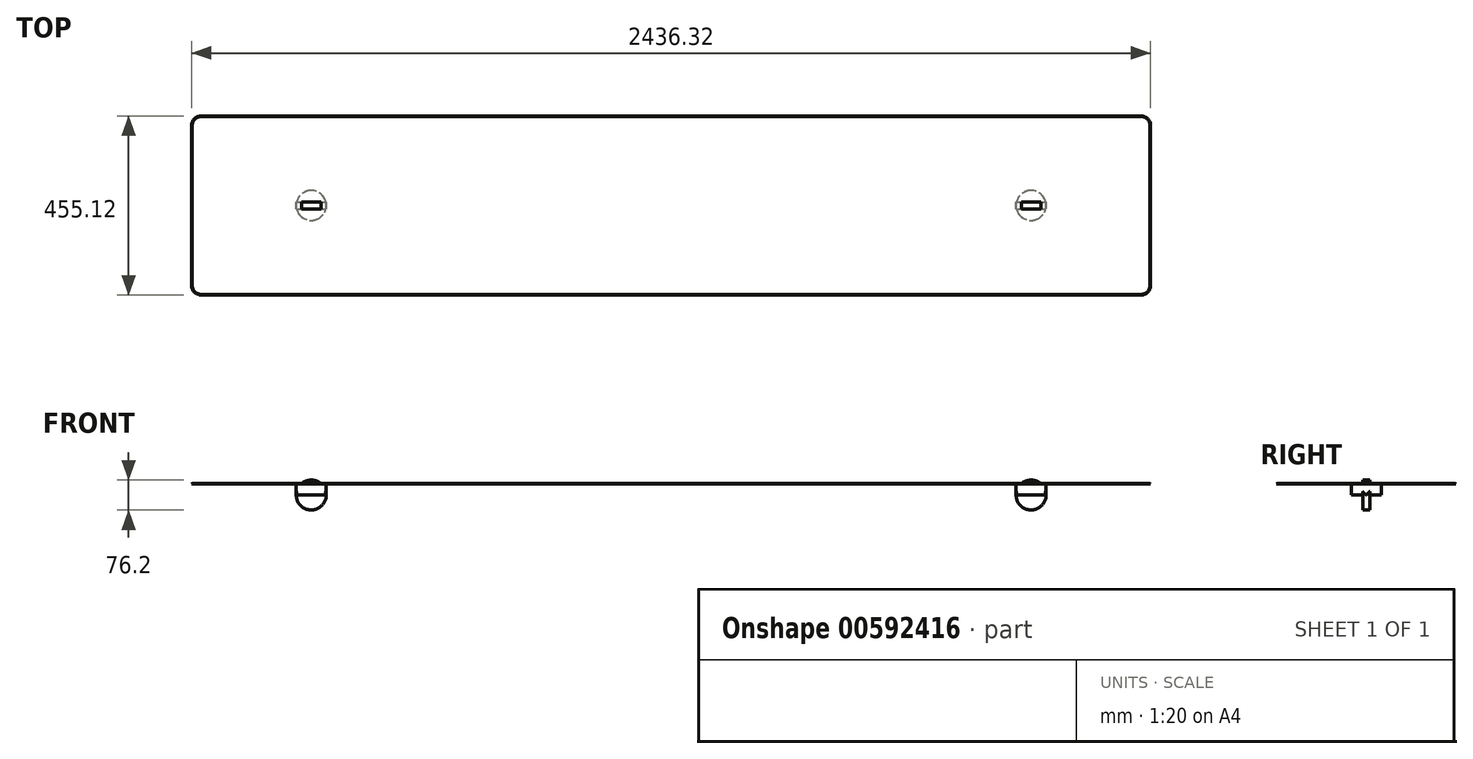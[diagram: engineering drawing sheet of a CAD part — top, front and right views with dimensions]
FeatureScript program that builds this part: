
annotation { "Feature Type Name" : "Feature", "Feature Type Description" : "" }
export const myFeature = defineFeature(function(context is Context, id is Id, definition is map)
    precondition{}
    {
        {
            assignVariable(context, id + "F0", {"name" : "depth", "anyValue" : 18});
        }
        {
            assignVariable(context, id + "F1", {"name" : "height", "anyValue" : 29});
        }
        {
            var Q0;
            Q0=qCreatedBy(makeId("Top.planeOp"),FACE);
            var sketch = newSketch(context, id + "F2", { "sketchPlane" : qUnion([Q0])});
            skLineSegment(sketch, "E0.bottom", {"start": v(1219.2, -228.6) * mm, "end": v(-1219.2, -228.6) * mm});
            skLineSegment(sketch, "E0.top", {"start": v(1219.2, 228.6) * mm, "end": v(-1219.2, 228.6) * mm});
            skLineSegment(sketch, "E0.left", {"start": v(1219.2, -228.6) * mm, "end": v(1219.2, 228.6) * mm});
            skLineSegment(sketch, "E0.right", {"start": v(-1219.2, -228.6) * mm, "end": v(-1219.2, 228.6) * mm});
            skPoint(sketch, "E0.middle", {"position": v(0, 0) * mm});
            skLineSegment(sketch, "E1", {"start": v(-1219.2, 0) * mm, "end": v(-914.4, 0) * mm, "construction": true});
            skLineSegment(sketch, "E2", {"start": v(-914.4, 0) * mm, "end": v(914.4, 0) * mm, "construction": true});
            skLineSegment(sketch, "E3", {"start": v(914.4, 0) * mm, "end": v(1219.2, 0) * mm, "construction": true});
            skCircle(sketch, "E4", {"center": v(-914.4, 0) * mm, "radius": 38.1 * mm});
            skCircle(sketch, "E5", {"center": v(914.4, 0) * mm, "radius": 38.1 * mm});
            skSolve(sketch);
        }
        {
            var Q0;
            Q0=makeQuery(id+"F2.imprint","IMPRINT",FACE,{"disambiguationData":[TD([[makeQuery(id+"F2.imprint","IMPRINT",EDGE,{"derivedFrom":sQuery(id+"F2.wireOp",EDGE,"E0.bottom")}),-1.0]])]});
            var Q1;
            Q1=makeQuery(id+"F2.imprint","IMPRINT",FACE,{"disambiguationData":[TD([[makeQuery(id+"F2.imprint","IMPRINT",EDGE,{"derivedFrom":sQuery(id+"F2.wireOp",EDGE,"E4")}),1.0]])]});
            var Q2;
            Q2=makeQuery(id+"F2.imprint","IMPRINT",FACE,{"disambiguationData":[TD([[makeQuery(id+"F2.imprint","IMPRINT",EDGE,{"derivedFrom":sQuery(id+"F2.wireOp",EDGE,"E5")}),1.0]])]});
            extrude(context, id + "F3", {"entities" : qUnion([Q0, Q1, Q2]), "depth" : (getVariable(context, 'height')) * mm, "offsetDistance" : 25.4 * mm, "hasSecondDirection" : true, "secondDirectionOppositeDirection" : false, "secondDirectionDepth" : (getVariable(context, 'height') - 1.5) * mm});
        }
        {
            var Q0;
            Q0=makeQuery(id+"F2.imprint","IMPRINT",FACE,{"disambiguationData":[TD([[makeQuery(id+"F2.imprint","IMPRINT",EDGE,{"derivedFrom":sQuery(id+"F2.wireOp",EDGE,"E4")}),1.0]])]});
            var Q1;
            Q1=makeQuery(id+"F2.imprint","IMPRINT",FACE,{"disambiguationData":[TD([[makeQuery(id+"F2.imprint","IMPRINT",EDGE,{"derivedFrom":sQuery(id+"F2.wireOp",EDGE,"E5")}),1.0]])]});
            var Q2;
            Q2=sQuery(id+"F2.wireOp",EDGE,"E4");
            var Q3;
            Q3=sQuery(id+"F2.wireOp",EDGE,"E5");
            extrude(context, id + "F4", {"entities" : qUnion([Q0, Q1]), "operationType" : NewBodyOperationType.ADD, "surfaceEntities" : qUnion([Q2, Q3]), "depth" : (getVariable(context, 'height')) * mm, "offsetDistance" : 25.4 * mm});
        }
        {
            var Q0;
            Q0=qCreatedBy(makeId("Front.planeOp"),FACE);
            var sketch = newSketch(context, id + "F5", { "sketchPlane" : qUnion([Q0])});
            skLineSegment(sketch, "E6", {"start": v(0, 0) * mm, "end": v(-914.4, 0) * mm, "construction": true});
            skLineSegment(sketch, "E7", {"start": v(0, 0) * mm, "end": v(914.4, 0) * mm, "construction": true});
            skCircle(sketch, "E8", {"center": v(-914.4, 0) * mm, "radius": 38.1 * mm});
            skCircle(sketch, "E9", {"center": v(914.4, 0) * mm, "radius": 38.1 * mm});
            skSolve(sketch);
        }
        {
            var Q0;
            Q0=makeQuery(id+"F5.imprint","IMPRINT",FACE,{"disambiguationData":[TD([[makeQuery(id+"F5.imprint","IMPRINT",EDGE,{"derivedFrom":sQuery(id+"F5.wireOp",EDGE,"E8")}),1.0]])]});
            var Q1;
            Q1=makeQuery(id+"F5.imprint","IMPRINT",FACE,{"disambiguationData":[TD([[makeQuery(id+"F5.imprint","IMPRINT",EDGE,{"derivedFrom":sQuery(id+"F5.wireOp",EDGE,"E9")}),1.0]])]});
            extrude(context, id + "F6", {"entities" : qUnion([Q0, Q1]), "operationType" : NewBodyOperationType.ADD, "depth" : (getVariable(context, 'depth') / 2) * mm, "offsetDistance" : 25.4 * mm, "hasSecondDirection" : true, "secondDirectionOppositeDirection" : true, "secondDirectionDepth" : (getVariable(context, 'depth') / 2) * mm});
        }
        {
            var Q0;
            Q0=makeQuery(id+"F3.opExtrude","SWEPT_EDGE",EDGE,{"disambiguationData":[OSD([sQuery(id+"F2.wireOp",EDGE,"E0.bottom"),sQuery(id+"F2.wireOp",EDGE,"E0.left")])]});
            var Q1;
            Q1=makeQuery(id+"F3.opExtrude","SWEPT_EDGE",EDGE,{"disambiguationData":[OSD([sQuery(id+"F2.wireOp",EDGE,"E0.top"),sQuery(id+"F2.wireOp",EDGE,"E0.left")])]});
            var Q2;
            Q2=makeQuery(id+"F3.opExtrude","SWEPT_EDGE",EDGE,{"disambiguationData":[OSD([sQuery(id+"F2.wireOp",EDGE,"E0.bottom"),sQuery(id+"F2.wireOp",EDGE,"E0.right")])]});
            var Q3;
            Q3=makeQuery(id+"F3.opExtrude","SWEPT_EDGE",EDGE,{"disambiguationData":[OSD([sQuery(id+"F2.wireOp",EDGE,"E0.top"),sQuery(id+"F2.wireOp",EDGE,"E0.right")])]});
            fillet(context, id + "F7", {"entities" : qUnion([Q0, Q1, Q2, Q3]), "radius" : 25.4 * mm, "tangentPropagation" : true, "allowEdgeOverflow" : false});
        }
        {
            var Q0;
            Q0=makeQuery(id+"F3.opExtrude","CAP_EDGE",EDGE,{"disambiguationData":[OSD([sQuery(id+"F2.wireOp",EDGE,"E0.right")])],"isStart":false});
            var Q1;
            {var subQ0=sQuery(id+"F2.wireOp",EDGE,"E0.right");var subQ1=sQuery(id+"F2.wireOp",EDGE,"E0.top");Q1=makeQuery(id+"F7.opFillet","BLEND_EDGE",EDGE,{"blendedFrom":[makeQuery(id+"F3.opExtrude","SWEPT_EDGE",EDGE,{"disambiguationData":[OSD([subQ1,subQ0])]}),makeQuery(id+"F3.opExtrude","CAP_FACE",FACE,{"disambiguationData":[OSD([sQuery(id+"F2.wireOp",EDGE,"E0.bottom"),subQ1,sQuery(id+"F2.wireOp",EDGE,"E0.left"),subQ0])],"isStart":false})],"blendedInto":[makeQuery(id+"F3.opExtrude","CAP_FACE",FACE,{"disambiguationData":[OSD([sQuery(id+"F2.wireOp",EDGE,"E0.bottom"),subQ1,sQuery(id+"F2.wireOp",EDGE,"E0.left"),subQ0])],"isStart":false})]});}
            var Q2;
            Q2=makeQuery(id+"F3.opExtrude","CAP_EDGE",EDGE,{"disambiguationData":[OSD([sQuery(id+"F2.wireOp",EDGE,"E0.top")])],"isStart":false});
            var Q3;
            {var subQ0=sQuery(id+"F2.wireOp",EDGE,"E0.right");var subQ1=sQuery(id+"F2.wireOp",EDGE,"E0.bottom");Q3=makeQuery(id+"F7.opFillet","BLEND_EDGE",EDGE,{"blendedFrom":[makeQuery(id+"F3.opExtrude","SWEPT_EDGE",EDGE,{"disambiguationData":[OSD([subQ1,subQ0])]}),makeQuery(id+"F3.opExtrude","CAP_FACE",FACE,{"disambiguationData":[OSD([subQ1,sQuery(id+"F2.wireOp",EDGE,"E0.top"),sQuery(id+"F2.wireOp",EDGE,"E0.left"),subQ0])],"isStart":false})],"blendedInto":[makeQuery(id+"F3.opExtrude","CAP_FACE",FACE,{"disambiguationData":[OSD([subQ1,sQuery(id+"F2.wireOp",EDGE,"E0.top"),sQuery(id+"F2.wireOp",EDGE,"E0.left"),subQ0])],"isStart":false})]});}
            var Q4;
            Q4=makeQuery(id+"F3.opExtrude","CAP_EDGE",EDGE,{"disambiguationData":[OSD([sQuery(id+"F2.wireOp",EDGE,"E0.bottom")])],"isStart":false});
            var Q5;
            Q5=makeQuery(id+"F3.opExtrude","CAP_EDGE",EDGE,{"disambiguationData":[OSD([sQuery(id+"F2.wireOp",EDGE,"E0.left")])],"isStart":false});
            var Q6;
            {var subQ0=sQuery(id+"F2.wireOp",EDGE,"E0.left");var subQ1=sQuery(id+"F2.wireOp",EDGE,"E0.top");Q6=makeQuery(id+"F7.opFillet","BLEND_EDGE",EDGE,{"blendedFrom":[makeQuery(id+"F3.opExtrude","SWEPT_EDGE",EDGE,{"disambiguationData":[OSD([subQ1,subQ0])]}),makeQuery(id+"F3.opExtrude","CAP_FACE",FACE,{"disambiguationData":[OSD([sQuery(id+"F2.wireOp",EDGE,"E0.bottom"),subQ1,subQ0,sQuery(id+"F2.wireOp",EDGE,"E0.right")])],"isStart":false})],"blendedInto":[makeQuery(id+"F3.opExtrude","CAP_FACE",FACE,{"disambiguationData":[OSD([sQuery(id+"F2.wireOp",EDGE,"E0.bottom"),subQ1,subQ0,sQuery(id+"F2.wireOp",EDGE,"E0.right")])],"isStart":false})]});}
            var Q7;
            {var subQ0=sQuery(id+"F2.wireOp",EDGE,"E0.left");var subQ1=sQuery(id+"F2.wireOp",EDGE,"E0.bottom");Q7=makeQuery(id+"F7.opFillet","BLEND_EDGE",EDGE,{"blendedFrom":[makeQuery(id+"F3.opExtrude","SWEPT_EDGE",EDGE,{"disambiguationData":[OSD([subQ1,subQ0])]}),makeQuery(id+"F3.opExtrude","CAP_FACE",FACE,{"disambiguationData":[OSD([subQ1,sQuery(id+"F2.wireOp",EDGE,"E0.top"),subQ0,sQuery(id+"F2.wireOp",EDGE,"E0.right")])],"isStart":false})],"blendedInto":[makeQuery(id+"F3.opExtrude","CAP_FACE",FACE,{"disambiguationData":[OSD([subQ1,sQuery(id+"F2.wireOp",EDGE,"E0.top"),subQ0,sQuery(id+"F2.wireOp",EDGE,"E0.right")])],"isStart":false})]});}
            chamfer(context, id + "F8", {"entities" : qUnion([Q0, Q1, Q2, Q3, Q4, Q5, Q6, Q7]), "width" : 2.54 * mm, "tangentPropagation" : true});
        }
    });
